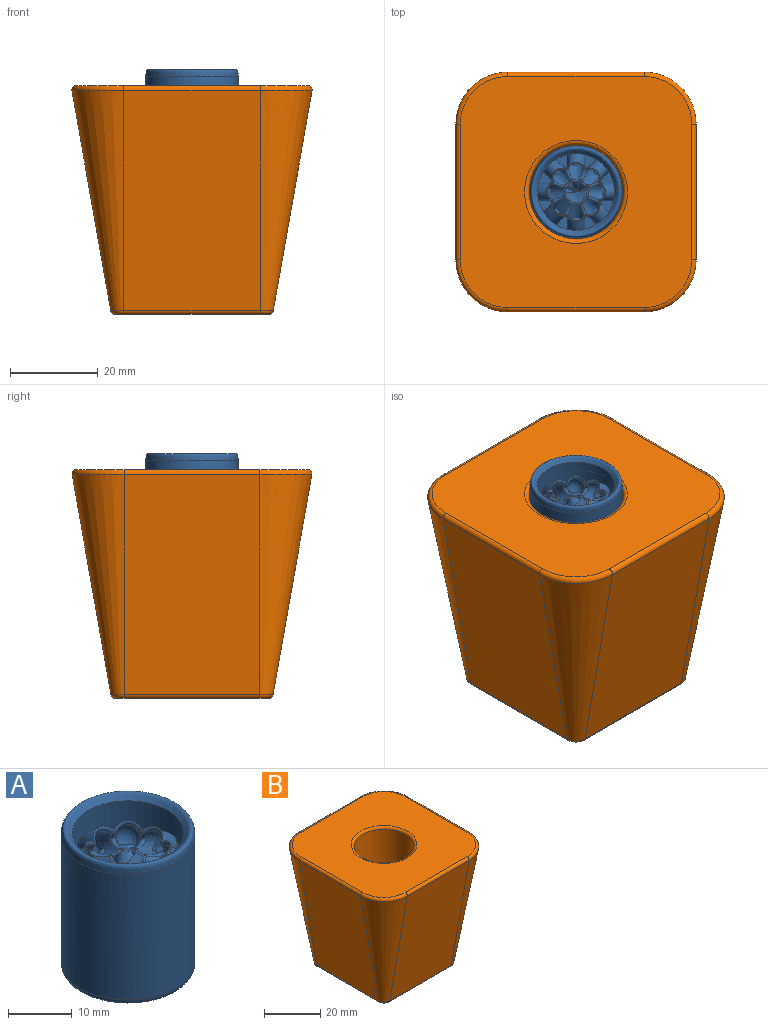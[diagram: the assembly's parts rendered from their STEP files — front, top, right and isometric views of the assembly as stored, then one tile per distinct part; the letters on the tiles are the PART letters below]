
ASSEMBLY  parts=2 mates=1
PART A: 142 faces, bbox 21x21x27.8 mm
  f0: bspline ~4x3.46mm, area 0mm2, adj f1,f140,f141
  f1: bspline ~8.05x8mm, area 71.6mm2, adj f0,f2,f135,f136,f137,f138,f139,f141
  f2: bspline ~11.35x11.35mm, area 71.6mm2, adj f1,f3,f130,f131,f132,f133,f134,f140
  f3: bspline ~8.05x8mm, area 71.6mm2, adj f2,f4,f124,f125,f126,f127,f128,f129
  f4: bspline ~11.35x11.35mm, area 71.6mm2, adj f3,f5,f118,f119,f120,f121,f122,f123
  f5: bspline ~8.05x8mm, area 71.6mm2, adj f4,f6,f112,f113,f114,f115,f116,f117
  f6: bspline ~11.35x11.35mm, area 71.6mm2, adj f5,f7,f106,f107,f108,f109,f110,f111
  f7: bspline ~8.05x8mm, area 71.6mm2, adj f6,f8,f101,f102,f103,f104,f105,f137
  f8: bspline ~4x3.46mm, area 0mm2, adj f7,f9,f101
  f9: bspline ~4.71x4.71mm, area 0mm2, adj f8,f10,f137
  f10: bspline ~5.39x4.99mm, area 0.2mm2, adj f9,f11,f101,f137
  f11: bspline ~12.67x12.67mm, area 92mm2, adj f10,f12,f14,f104,f137,f138
  f12: bspline ~5.39x4.99mm, area 0.2mm2, adj f11,f13,f135,f137
  f13: bspline ~4.71x4.71mm, area 0mm2, adj f12,f136,f137
  f14: bspline ~11.41x11.41mm, area 46.8mm2, adj f11,f15,f98,f99,f100
  f15: bspline ~3.59x3.51mm, area 4.5mm2, adj f14,f16,f96,f97
  f16: revolved ~17.41x17.41mm, area 0mm2, adj f15,f17,f53,f90,f91,f92,f93,f94
  f17: bspline ~4.59x1.88mm, area 0mm2, adj f16,f18,f52,f96
  f18: sphere r=0.5mm, area 0.4mm2, adj f17,f19,f95
  f19: bspline ~3.6x2.17mm, area 4.4mm2, adj f18,f20,f51,f52
  f20: bspline ~11.41x11.41mm, area 46.8mm2, adj f19,f21,f49,f95,f133
  f21: bspline ~2.03x1.91mm, area 0.9mm2, adj f20,f22,f46,f51
  f22: sphere r=0.5mm, area 0mm2, adj f21,f23,f49
  f23: bspline ~2.55x0.77mm, area 0.9mm2, adj f22,f24,f45,f46
  f24: bspline ~8.13x8mm, area 46.8mm2, adj f23,f25,f49,f94,f128
  f25: bspline ~3.78x2.16mm, area 4.4mm2, adj f24,f26,f27,f45
  f26: sphere r=0.5mm, area 0.3mm2, adj f25,f93,f94
  f27: bspline ~11.41x11.41mm, area 46.8mm2, adj f25,f28,f43,f93,f122
  f28: bspline ~2.03x1.91mm, area 0.9mm2, adj f27,f29,f45,f46
  f29: sphere r=0.5mm, area 0mm2, adj f28,f30,f43
  f30: bspline ~2.55x0.77mm, area 0.9mm2, adj f29,f31,f42,f46
  f31: bspline ~8.13x8mm, area 46.8mm2, adj f30,f32,f43,f92,f116
  f32: bspline ~3.78x2.16mm, area 4.4mm2, adj f31,f33,f34,f42
  f33: sphere r=0.5mm, area 0.3mm2, adj f32,f91,f92
  f34: bspline ~11.41x11.41mm, area 46.8mm2, adj f32,f35,f40,f91,f110
  f35: bspline ~2.03x1.91mm, area 0.9mm2, adj f34,f36,f42,f46
  f36: sphere r=0.5mm, area 0.1mm2, adj f35,f37,f40
  f37: bspline ~2.55x0.77mm, area 0.9mm2, adj f36,f38,f39,f46
  f38: bspline ~8.13x8mm, area 46.8mm2, adj f37,f40,f90,f98,f104
  f39: sphere r=0.5mm, area 0.2mm2, adj f37,f98,f99
  f40: bspline ~3.78x2.16mm, area 4.4mm2, adj f34,f36,f38,f41
  f41: sphere r=0.5mm, area 0.3mm2, adj f40,f90,f91
  f42: sphere r=0.5mm, area 0mm2, adj f30,f32,f35
  f43: bspline ~3.78x2.16mm, area 4.4mm2, adj f27,f29,f31,f44
  f44: sphere r=0.5mm, area 0.3mm2, adj f43,f92,f93
  f45: sphere r=0.5mm, area 0mm2, adj f23,f25,f28
  f46: revolved ~7.39x7.39mm, area 15.4mm2, adj f21,f23,f28,f30,f35,f37,f47,f99
  f47: bspline ~2.55x0.77mm, area 0.9mm2, adj f46,f48,f51,f52
  f48: sphere r=0.5mm, area 0.2mm2, adj f47,f99,f100
  f49: bspline ~3.78x2.16mm, area 4.4mm2, adj f20,f22,f24,f50
  f50: sphere r=0.5mm, area 0.3mm2, adj f49,f94,f95
  f51: sphere r=0.5mm, area 0.2mm2, adj f19,f21,f47
  f52: bspline ~8.13x8mm, area 46.8mm2, adj f17,f19,f47,f100,f138
  f53: bspline ~21x21mm, area 210.7mm2, adj f16,f54
  f54: cylinder r=10.5mm len=24.01mm, axis (0,0,-1), area 1583.9mm2, adj f53,f55
  f55: bspline ~21x21mm, area 103.6mm2, adj f54,f56
  f56: plane 19.01x19.01mm, normal (0,0,-1), area 261.5mm2, adj f55,f57,f83,f84,f85,f86,f87,f88
  f57: bspline ~2.63x0.92mm, area 1.7mm2, adj f56,f58,f82,f129
  f58: sphere r=0.5mm, area 0mm2, adj f57,f59,f89
  f59: bspline ~7.54x6.19mm, area 8.1mm2, adj f58,f60,f81,f129,f134
  f60: bspline ~0.33x0.33mm, area 0.1mm2, adj f59,f61,f63,f81
  f61: bspline ~7.54x6.19mm, area 8.1mm2, adj f60,f62,f63,f134,f139
  f62: sphere r=0.5mm, area 0mm2, adj f61,f88,f89
  f63: bspline ~0.37x0.27mm, area 0.1mm2, adj f60,f61,f64,f79
  f64: bspline ~0.33x0.33mm, area 0.1mm2, adj f63,f65,f68,f79
  f65: bspline ~7.54x6.19mm, area 8.1mm2, adj f64,f66,f67,f68,f105
  f66: bspline ~10.24x9.81mm, area 85.6mm2, adj f65,f79,f87,f137
  f67: sphere r=0.5mm, area 0mm2, adj f65,f86,f87
  f68: bspline ~0.37x0.27mm, area 0.1mm2, adj f64,f65,f69,f71
  f69: bspline ~7.54x6.19mm, area 8.1mm2, adj f68,f70,f71,f105,f111
  f70: sphere r=0.5mm, area 0mm2, adj f69,f85,f86
  f71: bspline ~0.33x0.33mm, area 0.1mm2, adj f68,f69,f72,f74
  f72: bspline ~7.54x6.19mm, area 8.1mm2, adj f71,f73,f74,f111,f117
  f73: sphere r=0.5mm, area 0mm2, adj f72,f84,f85
  f74: bspline ~0.37x0.27mm, area 0.1mm2, adj f71,f72,f75,f77
  f75: bspline ~7.54x6.19mm, area 8.1mm2, adj f74,f76,f77,f117,f123
  f76: sphere r=0.5mm, area 0mm2, adj f75,f83,f84
  f77: bspline ~0.33x0.33mm, area 0.1mm2, adj f74,f75,f78,f81
  f78: bspline ~7.54x6.19mm, area 8.1mm2, adj f77,f81,f82,f123,f129
  f79: bspline ~7.54x6.19mm, area 8.1mm2, adj f63,f64,f66,f80,f139
  f80: sphere r=0.5mm, area 0mm2, adj f79,f87,f88
  f81: bspline ~0.37x0.27mm, area 0.1mm2, adj f59,f60,f77,f78
  f82: sphere r=0.5mm, area 0mm2, adj f57,f78,f83
  f83: bspline ~2.01x2mm, area 1.7mm2, adj f56,f76,f82,f123
  f84: bspline ~2.63x0.92mm, area 1.7mm2, adj f56,f73,f76,f117
  f85: bspline ~2.01x2mm, area 1.7mm2, adj f56,f70,f73,f111
  f86: bspline ~2.63x0.92mm, area 1.7mm2, adj f56,f67,f70,f105
  f87: bspline ~2.01x2mm, area 1.7mm2, adj f56,f66,f67,f80
  f88: bspline ~2.63x0.92mm, area 1.7mm2, adj f56,f62,f80,f139
  f89: bspline ~2.01x2mm, area 1.7mm2, adj f56,f58,f62,f134
  f90: bspline ~4.59x1.88mm, area 4.5mm2, adj f16,f38,f41,f97
  f91: bspline ~3.59x3.51mm, area 4.5mm2, adj f16,f33,f34,f41
  f92: bspline ~4.59x1.88mm, area 4.5mm2, adj f16,f31,f33,f44
  f93: bspline ~3.59x3.51mm, area 4.5mm2, adj f16,f26,f27,f44
  f94: bspline ~4.59x1.88mm, area 4.5mm2, adj f16,f24,f26,f50
  f95: bspline ~3.59x3.51mm, area 4.5mm2, adj f16,f18,f20,f50
  f96: sphere r=0.5mm, area 0.4mm2, adj f15,f17,f100
  f97: sphere r=0.5mm, area 0.3mm2, adj f15,f90,f98
  f98: bspline ~3.78x2.16mm, area 4.4mm2, adj f14,f38,f39,f97
  f99: bspline ~2.03x1.91mm, area 0.9mm2, adj f14,f39,f46,f48
  f100: bspline ~3.78x2.16mm, area 4.4mm2, adj f14,f48,f52,f96
  f101: bspline ~6.36x6.36mm, area 0.2mm2, adj f7,f8,f10,f104
  f102: bspline ~6.36x6.36mm, area 0.2mm2, adj f7,f103,f104,f107
  f103: bspline ~4x3.46mm, area 0mm2, adj f7,f102,f106
  f104: bspline ~9.92x8.95mm, area 92mm2, adj f7,f11,f38,f101,f102,f110
  f105: bspline ~12.23x10.24mm, area 85.6mm2, adj f7,f65,f69,f86
  f106: bspline ~4.71x4.71mm, area 0mm2, adj f6,f103,f107
  f107: bspline ~5.39x4.99mm, area 0.2mm2, adj f6,f102,f106,f110
  f108: bspline ~5.39x4.99mm, area 0.2mm2, adj f6,f109,f110,f113
  f109: bspline ~4.71x4.71mm, area 0mm2, adj f6,f108,f112
  f110: bspline ~12.67x12.67mm, area 92mm2, adj f6,f34,f104,f107,f108,f116
  f111: bspline ~10.24x9.81mm, area 85.6mm2, adj f6,f69,f72,f85
  f112: bspline ~4x3.46mm, area 0mm2, adj f5,f109,f113
  f113: bspline ~6.36x6.36mm, area 0.2mm2, adj f5,f108,f112,f116
  f114: bspline ~6.36x6.36mm, area 0.2mm2, adj f5,f115,f116,f119
  f115: bspline ~4x3.46mm, area 0mm2, adj f5,f114,f118
  f116: bspline ~9.92x8.95mm, area 92mm2, adj f5,f31,f110,f113,f114,f122
  f117: bspline ~12.23x10.24mm, area 85.6mm2, adj f5,f72,f75,f84
  f118: bspline ~4.71x4.71mm, area 0mm2, adj f4,f115,f119
  f119: bspline ~5.39x4.99mm, area 0.2mm2, adj f4,f114,f118,f122
  f120: bspline ~5.39x4.99mm, area 0.2mm2, adj f4,f121,f122,f125
  f121: bspline ~4.71x4.71mm, area 0mm2, adj f4,f120,f124
  f122: bspline ~12.67x12.67mm, area 92mm2, adj f4,f27,f116,f119,f120,f128
  f123: bspline ~10.24x9.81mm, area 85.6mm2, adj f4,f75,f78,f83
  f124: bspline ~4x3.46mm, area 0mm2, adj f3,f121,f125
  f125: bspline ~6.36x6.36mm, area 0.2mm2, adj f3,f120,f124,f128
  f126: bspline ~6.36x6.36mm, area 0.2mm2, adj f3,f127,f128,f131
  f127: bspline ~4x3.46mm, area 0mm2, adj f3,f126,f130
  f128: bspline ~9.92x8.95mm, area 92mm2, adj f3,f24,f122,f125,f126,f133
  f129: bspline ~12.23x10.24mm, area 85.6mm2, adj f3,f57,f59,f78
  f130: bspline ~4.71x4.71mm, area 0mm2, adj f2,f127,f131
  f131: bspline ~5.39x4.99mm, area 0.2mm2, adj f2,f126,f130,f133
  f132: bspline ~5.39x4.99mm, area 0.2mm2, adj f2,f133,f140,f141
  f133: bspline ~12.67x12.67mm, area 92mm2, adj f2,f20,f128,f131,f132,f138
  f134: bspline ~10.24x9.81mm, area 85.6mm2, adj f2,f59,f61,f89
  f135: bspline ~6.36x6.36mm, area 0.2mm2, adj f1,f12,f136,f138
  f136: bspline ~4x3.46mm, area 0mm2, adj f1,f13,f135
  f137: bspline ~11.35x11.35mm, area 71.6mm2, adj f1,f7,f9,f10,f11,f12,f13,f66
  f138: bspline ~9.92x8.95mm, area 92mm2, adj f1,f11,f52,f133,f135,f141
  f139: bspline ~12.23x10.24mm, area 85.6mm2, adj f1,f61,f79,f88
  f140: bspline ~4.71x4.71mm, area 0mm2, adj f0,f2,f132
  f141: bspline ~6.36x6.36mm, area 0.2mm2, adj f0,f1,f132,f138
PART B: 42 faces, bbox 56.6x56.5x52 mm
  f0: plane 50x31mm, normal (0,0.98,-0.17), area 1573.9mm2, adj f1,f7,f11,f19
  f1: cone r=12mm half-angle=10deg, axis (0,0,1), area 589mm2, adj f0,f2,f12,f20
  f2: plane 50x30.9mm, normal (-0.98,0,-0.17), area 1568.8mm2, adj f1,f3,f14,f22
  f3: cone r=12mm half-angle=10deg, axis (0,0,1), area 589mm2, adj f2,f4,f16,f24
  f4: plane 50x31mm, normal (0,-0.98,-0.17), area 1573.9mm2, adj f3,f5,f18,f26
  f5: cone r=12mm half-angle=10deg, axis (0,0,1), area 589mm2, adj f4,f6,f17,f25
  f6: plane 50x30.9mm, normal (0.98,0,-0.17), area 1568.8mm2, adj f5,f7,f15,f23
  f7: cone r=12mm half-angle=10deg, axis (0,0,1), area 589mm2, adj f0,f6,f13,f21
  f8: plane 34.98x34.88mm, normal (0,0,-1), area 1217mm2, adj f19,f20,f21,f22,f23,f24,f25,f26
  f9: plane 52.62x52.52mm, normal (0,0,1), area 2232.9mm2, adj f11,f12,f13,f14,f15,f16,f17,f18
  f10: cylinder r=10.7mm len=22mm, axis (0,0,1), area 1479.1mm2, adj f27,f28
  f11: cylinder r=1mm len=31mm, axis (1,0,0), area 54.1mm2, adj f0,f9,f12,f13
  f12: torus R=10.81mm, axis (0,0,1), area 31.5mm2, adj f1,f9,f11,f14
  f13: torus R=10.81mm, axis (0,0,1), area 31.5mm2, adj f7,f9,f11,f15
  f14: cylinder r=1mm len=30.9mm, axis (0,1,0), area 53.9mm2, adj f2,f9,f12,f16
  f15: cylinder r=1mm len=30.9mm, axis (0,1,0), area 53.9mm2, adj f6,f9,f13,f17
  f16: torus R=10.81mm, axis (0,0,1), area 31.5mm2, adj f3,f9,f14,f18
  f17: torus R=10.81mm, axis (0,0,1), area 31.5mm2, adj f5,f9,f15,f18
  f18: cylinder r=1mm len=31mm, axis (1,0,0), area 54.1mm2, adj f4,f9,f16,f17
  f19: cylinder r=1mm len=31mm, axis (-1,0,0), area 43.3mm2, adj f0,f8,f20,f21
  f20: torus R=1.99mm, axis (0,0,1), area 5.7mm2, adj f1,f8,f19,f22
  f21: torus R=1.99mm, axis (0,0,1), area 5.7mm2, adj f7,f8,f19,f23
  f22: cylinder r=1mm len=30.9mm, axis (0,-1,0), area 43.1mm2, adj f2,f8,f20,f24
  f23: cylinder r=1mm len=30.9mm, axis (0,-1,0), area 43.1mm2, adj f6,f8,f21,f25
  f24: torus R=1.99mm, axis (0,0,1), area 5.7mm2, adj f3,f8,f22,f26
  f25: torus R=1.99mm, axis (0,0,1), area 5.7mm2, adj f5,f8,f23,f26
  f26: cylinder r=1mm len=31mm, axis (-1,0,0), area 43.3mm2, adj f4,f8,f24,f25
  f27: torus R=11.7mm, axis (0,0,1), area 109.2mm2, adj f9,f10
  f28: torus R=5.7mm, axis (0,0,1), area 438.4mm2, adj f10,f29
  f29: cylinder r=5.7mm len=11.4mm, axis (0,0,1), area 35.8mm2, adj f28,f41
  f30: plane 50x31mm, normal (0,-0.98,0.17), area 1573.9mm2, adj f31,f37,f38,f39
  f31: cone r=11.02mm half-angle=10deg, axis (0,0,1), area 510.4mm2, adj f30,f32,f38,f39
  f32: plane 50x30.9mm, normal (0.98,0,0.17), area 1568.8mm2, adj f31,f33,f38,f39
  f33: cone r=11.02mm half-angle=10deg, axis (0,0,1), area 510.4mm2, adj f32,f34,f38,f39
  f34: plane 50x31mm, normal (0,0.98,0.17), area 1573.9mm2, adj f33,f35,f38,f39
  f35: cone r=11.02mm half-angle=10deg, axis (0,0,1), area 510.4mm2, adj f34,f36,f38,f39
  f36: plane 50x30.9mm, normal (-0.98,0,0.17), area 1568.8mm2, adj f35,f37,f38,f39
  f37: cone r=11.02mm half-angle=10deg, axis (0,0,1), area 510.4mm2, adj f30,f36,f38,f39
  f38: plane 34.98x34.88mm, normal (0,0,1), area 1217mm2, adj f30,f31,f32,f33,f34,f35,f36,f37
  f39: plane 52.62x52.52mm, normal (0,0,-1), area 2232.9mm2, adj f30,f31,f32,f33,f34,f35,f36,f37
  f40: cylinder r=11.7mm len=23.4mm, axis (0,0,1), area 1617.3mm2, adj f39,f41
  f41: torus R=5.7mm, axis (0,0,1), area 563.7mm2, adj f29,f40
PLACE A t=(0,67.5,2.61)mm
PLACE B t=(0,67.5,25.61)mm
MATE fastened B.f10 <-> A.f54  axis (0,0,1) through (0,67.5,2.61)mm
